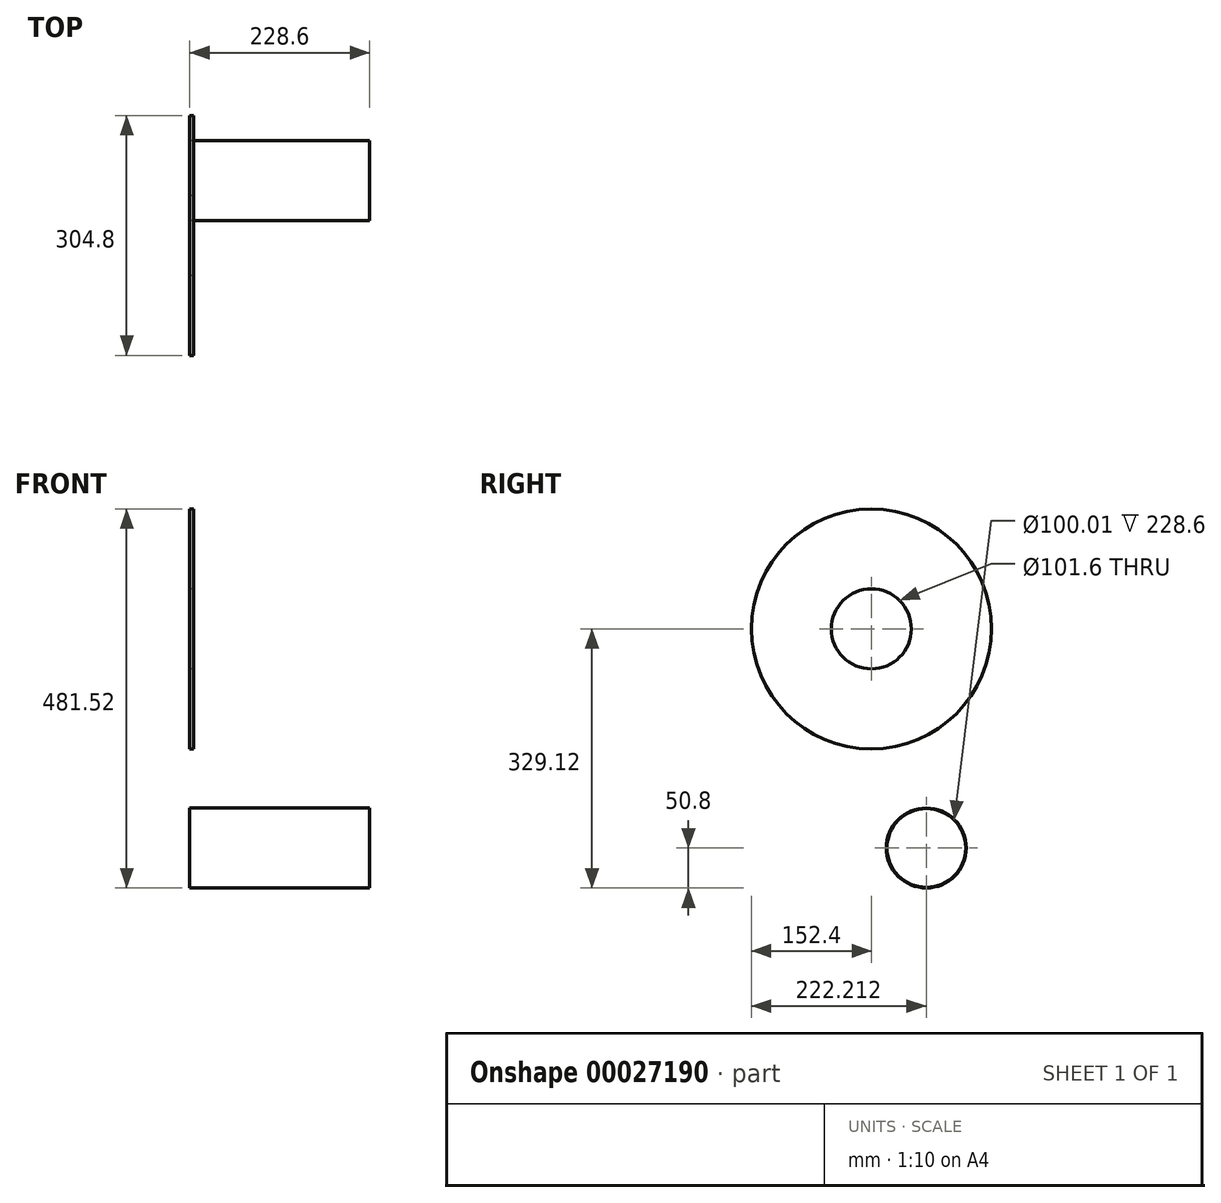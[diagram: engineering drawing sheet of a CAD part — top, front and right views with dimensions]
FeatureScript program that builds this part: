
annotation { "Feature Type Name" : "Feature", "Feature Type Description" : "" }
export const myFeature = defineFeature(function(context is Context, id is Id, definition is map)
    precondition{}
    {
        {
            var Q0;
            Q0=qCreatedBy(makeId("Right.planeOp"),FACE);
            var sketch = newSketch(context, id + "F0", { "sketchPlane" : qUnion([Q0])});
            skCircle(sketch, "E0", {"center": v(0, 0) * mm, "radius": 152.4 * mm});
            skCircle(sketch, "E1", {"center": v(0, 0) * mm, "radius": 50.8 * mm});
            skSolve(sketch);
        }
        {
            var Q0;
            Q0=makeQuery(id+"F0.imprint","IMPRINT",FACE,{"disambiguationData":[TD([[makeQuery(id+"F0.imprint","IMPRINT",EDGE,{"derivedFrom":sQuery(id+"F0.wireOp",EDGE,"E0")}),1.0]])]});
            extrude(context, id + "F1", {"entities" : qUnion([Q0]), "depth" : 4.75 * mm});
        }
        {
            var Q0;
            Q0=qCreatedBy(makeId("Right.planeOp"),FACE);
            var sketch = newSketch(context, id + "F2", { "sketchPlane" : qUnion([Q0])});
            skCircle(sketch, "E2", {"center": v(69.81, -278.32) * mm, "radius": 50.8 * mm});
            skCircle(sketch, "E3", {"center": v(69.81, -278.32) * mm, "radius": 50 * mm});
            skSolve(sketch);
        }
        {
            var Q0;
            Q0=makeQuery(id+"F2.imprint","IMPRINT",FACE,{"disambiguationData":[TD([[makeQuery(id+"F2.imprint","IMPRINT",EDGE,{"derivedFrom":sQuery(id+"F2.wireOp",EDGE,"E2")}),1.0]])]});
            extrude(context, id + "F3", {"entities" : qUnion([Q0]), "depth" : 228.6 * mm});
        }
    });
